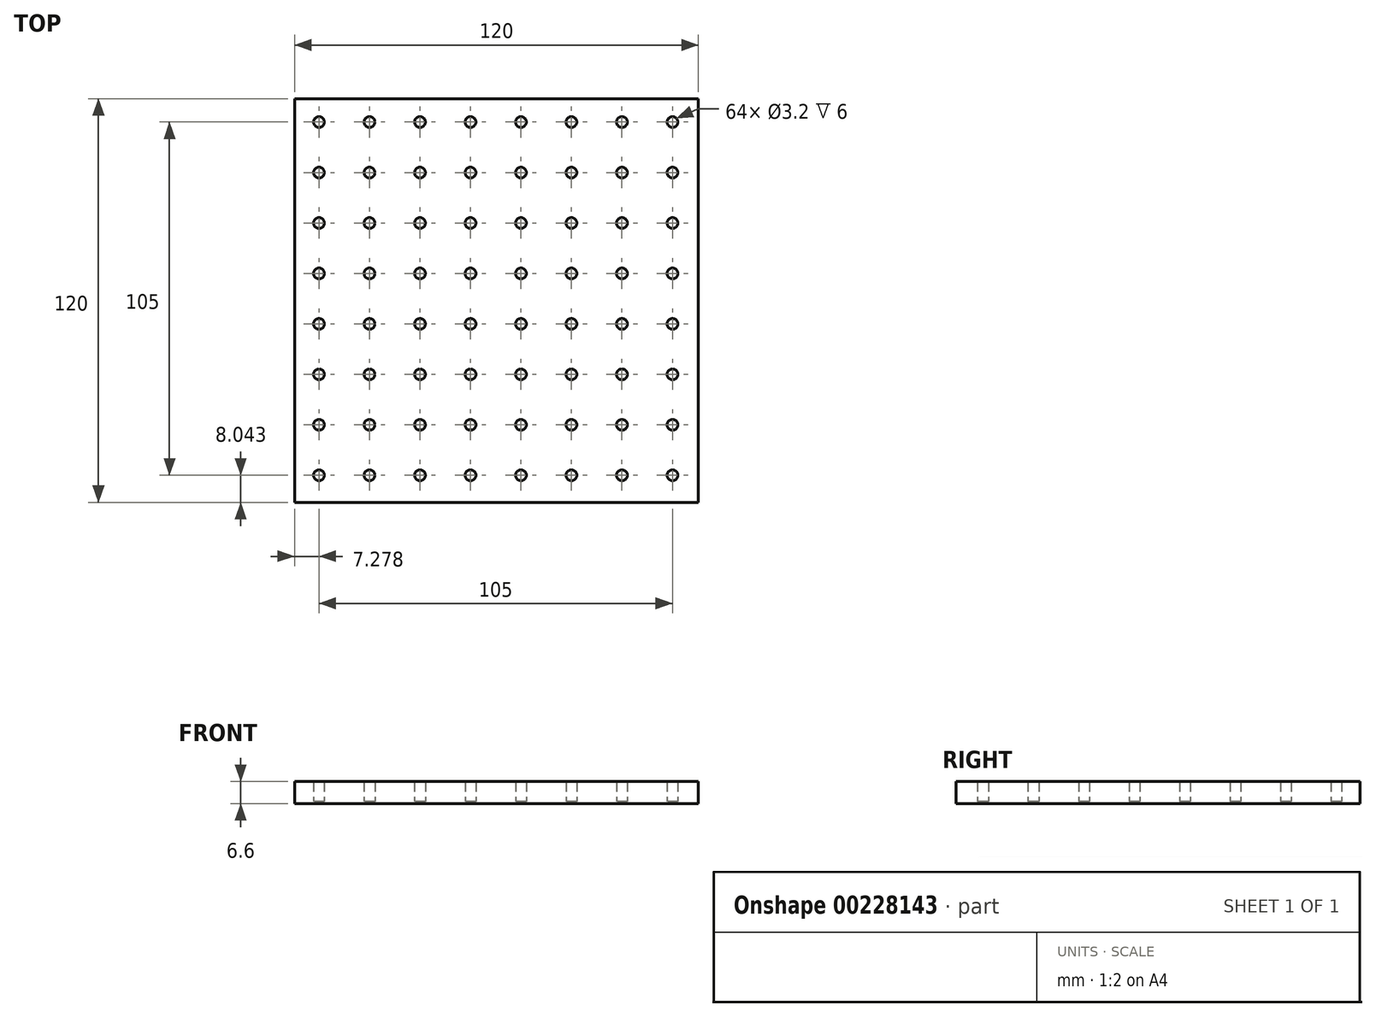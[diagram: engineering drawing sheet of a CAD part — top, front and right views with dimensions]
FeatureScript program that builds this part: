
annotation { "Feature Type Name" : "Feature", "Feature Type Description" : "" }
export const myFeature = defineFeature(function(context is Context, id is Id, definition is map)
    precondition{}
    {
        {
            var Q0;
            Q0=qCreatedBy(makeId("Top.planeOp"),FACE);
            var sketch = newSketch(context, id + "F0", { "sketchPlane" : qUnion([Q0])});
            skLineSegment(sketch, "E0.bottom", {"start": v(-60, 60) * mm, "end": v(60, 60) * mm});
            skLineSegment(sketch, "E0.top", {"start": v(-60, -60) * mm, "end": v(60, -60) * mm});
            skLineSegment(sketch, "E0.left", {"start": v(-60, 60) * mm, "end": v(-60, -60) * mm});
            skLineSegment(sketch, "E0.right", {"start": v(60, 60) * mm, "end": v(60, -60) * mm});
            skPoint(sketch, "E0.middle", {"position": v(0, 0) * mm});
            skCircle(sketch, "E1", {"center": v(-52.72, 53.04) * mm, "radius": 1.6 * mm});
            skCircle(sketch, "E2.0.1.0", {"center": v(-52.72, 38.04) * mm, "radius": 1.6 * mm});
            skCircle(sketch, "E2.0.2.0", {"center": v(-52.72, 23.04) * mm, "radius": 1.6 * mm});
            skCircle(sketch, "E2.0.3.0", {"center": v(-52.72, 8.04) * mm, "radius": 1.6 * mm});
            skCircle(sketch, "E2.0.4.0", {"center": v(-52.72, -6.96) * mm, "radius": 1.6 * mm});
            skCircle(sketch, "E2.0.5.0", {"center": v(-52.72, -21.96) * mm, "radius": 1.6 * mm});
            skCircle(sketch, "E2.0.6.0", {"center": v(-52.72, -36.96) * mm, "radius": 1.6 * mm});
            skCircle(sketch, "E2.0.7.0", {"center": v(-52.72, -51.96) * mm, "radius": 1.6 * mm});
            skCircle(sketch, "E2.1.0.0", {"center": v(-37.72, 53.04) * mm, "radius": 1.6 * mm});
            skCircle(sketch, "E2.1.1.0", {"center": v(-37.72, 38.04) * mm, "radius": 1.6 * mm});
            skCircle(sketch, "E2.1.2.0", {"center": v(-37.72, 23.04) * mm, "radius": 1.6 * mm});
            skCircle(sketch, "E2.1.3.0", {"center": v(-37.72, 8.04) * mm, "radius": 1.6 * mm});
            skCircle(sketch, "E2.1.4.0", {"center": v(-37.72, -6.96) * mm, "radius": 1.6 * mm});
            skCircle(sketch, "E2.1.5.0", {"center": v(-37.72, -21.96) * mm, "radius": 1.6 * mm});
            skCircle(sketch, "E2.1.6.0", {"center": v(-37.72, -36.96) * mm, "radius": 1.6 * mm});
            skCircle(sketch, "E2.1.7.0", {"center": v(-37.72, -51.96) * mm, "radius": 1.6 * mm});
            skCircle(sketch, "E2.2.0.0", {"center": v(-22.72, 53.04) * mm, "radius": 1.6 * mm});
            skCircle(sketch, "E2.2.1.0", {"center": v(-22.72, 38.04) * mm, "radius": 1.6 * mm});
            skCircle(sketch, "E2.2.2.0", {"center": v(-22.72, 23.04) * mm, "radius": 1.6 * mm});
            skCircle(sketch, "E2.2.3.0", {"center": v(-22.72, 8.04) * mm, "radius": 1.6 * mm});
            skCircle(sketch, "E2.2.4.0", {"center": v(-22.72, -6.96) * mm, "radius": 1.6 * mm});
            skCircle(sketch, "E2.2.5.0", {"center": v(-22.72, -21.96) * mm, "radius": 1.6 * mm});
            skCircle(sketch, "E2.2.6.0", {"center": v(-22.72, -36.96) * mm, "radius": 1.6 * mm});
            skCircle(sketch, "E2.2.7.0", {"center": v(-22.72, -51.96) * mm, "radius": 1.6 * mm});
            skCircle(sketch, "E2.3.0.0", {"center": v(-7.72, 53.04) * mm, "radius": 1.6 * mm});
            skCircle(sketch, "E2.3.1.0", {"center": v(-7.72, 38.04) * mm, "radius": 1.6 * mm});
            skCircle(sketch, "E2.3.2.0", {"center": v(-7.72, 23.04) * mm, "radius": 1.6 * mm});
            skCircle(sketch, "E2.3.3.0", {"center": v(-7.72, 8.04) * mm, "radius": 1.6 * mm});
            skCircle(sketch, "E2.3.4.0", {"center": v(-7.72, -6.96) * mm, "radius": 1.6 * mm});
            skCircle(sketch, "E2.3.5.0", {"center": v(-7.72, -21.96) * mm, "radius": 1.6 * mm});
            skCircle(sketch, "E2.3.6.0", {"center": v(-7.72, -36.96) * mm, "radius": 1.6 * mm});
            skCircle(sketch, "E2.3.7.0", {"center": v(-7.72, -51.96) * mm, "radius": 1.6 * mm});
            skCircle(sketch, "E2.4.0.0", {"center": v(7.28, 53.04) * mm, "radius": 1.6 * mm});
            skCircle(sketch, "E2.4.1.0", {"center": v(7.28, 38.04) * mm, "radius": 1.6 * mm});
            skCircle(sketch, "E2.4.2.0", {"center": v(7.28, 23.04) * mm, "radius": 1.6 * mm});
            skCircle(sketch, "E2.4.3.0", {"center": v(7.28, 8.04) * mm, "radius": 1.6 * mm});
            skCircle(sketch, "E2.4.4.0", {"center": v(7.28, -6.96) * mm, "radius": 1.6 * mm});
            skCircle(sketch, "E2.4.5.0", {"center": v(7.28, -21.96) * mm, "radius": 1.6 * mm});
            skCircle(sketch, "E2.4.6.0", {"center": v(7.28, -36.96) * mm, "radius": 1.6 * mm});
            skCircle(sketch, "E2.4.7.0", {"center": v(7.28, -51.96) * mm, "radius": 1.6 * mm});
            skCircle(sketch, "E2.5.0.0", {"center": v(22.28, 53.04) * mm, "radius": 1.6 * mm});
            skCircle(sketch, "E2.5.1.0", {"center": v(22.28, 38.04) * mm, "radius": 1.6 * mm});
            skCircle(sketch, "E2.5.2.0", {"center": v(22.28, 23.04) * mm, "radius": 1.6 * mm});
            skCircle(sketch, "E2.5.3.0", {"center": v(22.28, 8.04) * mm, "radius": 1.6 * mm});
            skCircle(sketch, "E2.5.4.0", {"center": v(22.28, -6.96) * mm, "radius": 1.6 * mm});
            skCircle(sketch, "E2.5.5.0", {"center": v(22.28, -21.96) * mm, "radius": 1.6 * mm});
            skCircle(sketch, "E2.5.6.0", {"center": v(22.28, -36.96) * mm, "radius": 1.6 * mm});
            skCircle(sketch, "E2.5.7.0", {"center": v(22.28, -51.96) * mm, "radius": 1.6 * mm});
            skCircle(sketch, "E2.6.0.0", {"center": v(37.28, 53.04) * mm, "radius": 1.6 * mm});
            skCircle(sketch, "E2.6.1.0", {"center": v(37.28, 38.04) * mm, "radius": 1.6 * mm});
            skCircle(sketch, "E2.6.2.0", {"center": v(37.28, 23.04) * mm, "radius": 1.6 * mm});
            skCircle(sketch, "E2.6.3.0", {"center": v(37.28, 8.04) * mm, "radius": 1.6 * mm});
            skCircle(sketch, "E2.6.4.0", {"center": v(37.28, -6.96) * mm, "radius": 1.6 * mm});
            skCircle(sketch, "E2.6.5.0", {"center": v(37.28, -21.96) * mm, "radius": 1.6 * mm});
            skCircle(sketch, "E2.6.6.0", {"center": v(37.28, -36.96) * mm, "radius": 1.6 * mm});
            skCircle(sketch, "E2.6.7.0", {"center": v(37.28, -51.96) * mm, "radius": 1.6 * mm});
            skCircle(sketch, "E2.7.0.0", {"center": v(52.28, 53.04) * mm, "radius": 1.6 * mm});
            skCircle(sketch, "E2.7.1.0", {"center": v(52.28, 38.04) * mm, "radius": 1.6 * mm});
            skCircle(sketch, "E2.7.2.0", {"center": v(52.28, 23.04) * mm, "radius": 1.6 * mm});
            skCircle(sketch, "E2.7.3.0", {"center": v(52.28, 8.04) * mm, "radius": 1.6 * mm});
            skCircle(sketch, "E2.7.4.0", {"center": v(52.28, -6.96) * mm, "radius": 1.6 * mm});
            skCircle(sketch, "E2.7.5.0", {"center": v(52.28, -21.96) * mm, "radius": 1.6 * mm});
            skCircle(sketch, "E2.7.6.0", {"center": v(52.28, -36.96) * mm, "radius": 1.6 * mm});
            skCircle(sketch, "E2.7.7.0", {"center": v(52.28, -51.96) * mm, "radius": 1.6 * mm});
            skLineSegment(sketch, "E2.direction1", {"start": v(-52.72, 53.04) * mm, "end": v(-37.72, 53.04) * mm, "construction": true});
            skLineSegment(sketch, "E2.direction2", {"start": v(-52.72, 53.04) * mm, "end": v(-52.72, 38.04) * mm, "construction": true});
            skSolve(sketch);
        }
        {
            var Q0;
            Q0=makeQuery(id+"F0.imprint","IMPRINT",FACE,{"disambiguationData":[TD([[makeQuery(id+"F0.imprint","IMPRINT",EDGE,{"derivedFrom":sQuery(id+"F0.wireOp",EDGE,"E0.bottom")}),-1.0]])]});
            extrude(context, id + "F1", {"entities" : qUnion([Q0]), "depth" : 6 * mm});
        }
        {
            var Q0;
            Q0=makeQuery(id+"F1.opExtrude","CAP_FACE",FACE,{"disambiguationData":[OSD([sQuery(id+"F0.wireOp",EDGE,"E0.bottom"),sQuery(id+"F0.wireOp",EDGE,"E0.top"),sQuery(id+"F0.wireOp",EDGE,"E0.left"),sQuery(id+"F0.wireOp",EDGE,"E0.right"),sQuery(id+"F0.wireOp",EDGE,"E1"),sQuery(id+"F0.wireOp",EDGE,"E2.0.1.0"),sQuery(id+"F0.wireOp",EDGE,"E2.0.2.0"),sQuery(id+"F0.wireOp",EDGE,"E2.0.3.0"),sQuery(id+"F0.wireOp",EDGE,"E2.0.4.0"),sQuery(id+"F0.wireOp",EDGE,"E2.0.5.0"),sQuery(id+"F0.wireOp",EDGE,"E2.0.6.0"),sQuery(id+"F0.wireOp",EDGE,"E2.0.7.0"),sQuery(id+"F0.wireOp",EDGE,"E2.1.0.0"),sQuery(id+"F0.wireOp",EDGE,"E2.1.1.0"),sQuery(id+"F0.wireOp",EDGE,"E2.1.2.0"),sQuery(id+"F0.wireOp",EDGE,"E2.1.3.0"),sQuery(id+"F0.wireOp",EDGE,"E2.1.4.0"),sQuery(id+"F0.wireOp",EDGE,"E2.1.5.0"),sQuery(id+"F0.wireOp",EDGE,"E2.1.6.0"),sQuery(id+"F0.wireOp",EDGE,"E2.1.7.0"),sQuery(id+"F0.wireOp",EDGE,"E2.2.0.0"),sQuery(id+"F0.wireOp",EDGE,"E2.2.1.0"),sQuery(id+"F0.wireOp",EDGE,"E2.2.2.0"),sQuery(id+"F0.wireOp",EDGE,"E2.2.3.0"),sQuery(id+"F0.wireOp",EDGE,"E2.2.4.0"),sQuery(id+"F0.wireOp",EDGE,"E2.2.5.0"),sQuery(id+"F0.wireOp",EDGE,"E2.2.6.0"),sQuery(id+"F0.wireOp",EDGE,"E2.2.7.0"),sQuery(id+"F0.wireOp",EDGE,"E2.3.0.0"),sQuery(id+"F0.wireOp",EDGE,"E2.3.1.0"),sQuery(id+"F0.wireOp",EDGE,"E2.3.2.0"),sQuery(id+"F0.wireOp",EDGE,"E2.3.3.0"),sQuery(id+"F0.wireOp",EDGE,"E2.3.4.0"),sQuery(id+"F0.wireOp",EDGE,"E2.3.5.0"),sQuery(id+"F0.wireOp",EDGE,"E2.3.6.0"),sQuery(id+"F0.wireOp",EDGE,"E2.3.7.0"),sQuery(id+"F0.wireOp",EDGE,"E2.4.0.0"),sQuery(id+"F0.wireOp",EDGE,"E2.4.1.0"),sQuery(id+"F0.wireOp",EDGE,"E2.4.2.0"),sQuery(id+"F0.wireOp",EDGE,"E2.4.3.0"),sQuery(id+"F0.wireOp",EDGE,"E2.4.4.0"),sQuery(id+"F0.wireOp",EDGE,"E2.4.5.0"),sQuery(id+"F0.wireOp",EDGE,"E2.4.6.0"),sQuery(id+"F0.wireOp",EDGE,"E2.4.7.0"),sQuery(id+"F0.wireOp",EDGE,"E2.5.0.0"),sQuery(id+"F0.wireOp",EDGE,"E2.5.1.0"),sQuery(id+"F0.wireOp",EDGE,"E2.5.2.0"),sQuery(id+"F0.wireOp",EDGE,"E2.5.3.0"),sQuery(id+"F0.wireOp",EDGE,"E2.5.4.0"),sQuery(id+"F0.wireOp",EDGE,"E2.5.5.0"),sQuery(id+"F0.wireOp",EDGE,"E2.5.6.0"),sQuery(id+"F0.wireOp",EDGE,"E2.5.7.0"),sQuery(id+"F0.wireOp",EDGE,"E2.6.0.0"),sQuery(id+"F0.wireOp",EDGE,"E2.6.1.0"),sQuery(id+"F0.wireOp",EDGE,"E2.6.2.0"),sQuery(id+"F0.wireOp",EDGE,"E2.6.3.0"),sQuery(id+"F0.wireOp",EDGE,"E2.6.4.0"),sQuery(id+"F0.wireOp",EDGE,"E2.6.5.0"),sQuery(id+"F0.wireOp",EDGE,"E2.6.6.0"),sQuery(id+"F0.wireOp",EDGE,"E2.6.7.0"),sQuery(id+"F0.wireOp",EDGE,"E2.7.0.0"),sQuery(id+"F0.wireOp",EDGE,"E2.7.1.0"),sQuery(id+"F0.wireOp",EDGE,"E2.7.2.0"),sQuery(id+"F0.wireOp",EDGE,"E2.7.3.0"),sQuery(id+"F0.wireOp",EDGE,"E2.7.4.0"),sQuery(id+"F0.wireOp",EDGE,"E2.7.5.0"),sQuery(id+"F0.wireOp",EDGE,"E2.7.6.0"),sQuery(id+"F0.wireOp",EDGE,"E2.7.7.0")])],"isStart":true});
            var sketch = newSketch(context, id + "F2", { "sketchPlane" : qUnion([Q0])});
            skLineSegment(sketch, "E3.bottom", {"start": v(-60, 60) * mm, "end": v(60, 60) * mm});
            skLineSegment(sketch, "E3.top", {"start": v(-60, -60) * mm, "end": v(60, -60) * mm});
            skLineSegment(sketch, "E3.left", {"start": v(-60, 60) * mm, "end": v(-60, -60) * mm});
            skLineSegment(sketch, "E3.right", {"start": v(60, 60) * mm, "end": v(60, -60) * mm});
            skSolve(sketch);
        }
        {
            var Q0;
            Q0 = qSketchRegion(id + "F2", true);
            extrude(context, id + "F3", {"entities" : qUnion([Q0]), "operationType" : NewBodyOperationType.ADD, "depth" : 0.6 * mm});
        }
    });
